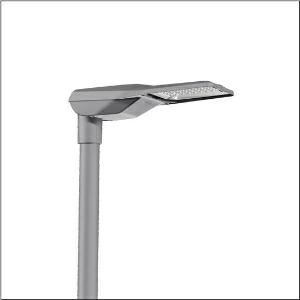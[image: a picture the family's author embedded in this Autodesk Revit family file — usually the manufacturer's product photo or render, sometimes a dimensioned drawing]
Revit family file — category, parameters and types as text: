
# Revit family: streetlight_sl_21_iq_mini___stw1_0a_5xe2e31g08gb_0d22
name_source: partatom
category: Lighting Fixtures
units: mm (PartAtom-declared; Revit-internal decimal feet)

## family parameters
Cut with Voids When Loaded = No
Host = Face
Light Source = No
Part Type = Normal
Room Calculation Point = No
Round Connector Dimension = Use Diameter
Shared = No

## types (1)
- --- (1 x LED, 5680 lm, 37.1 W, 3000K)
    Apparent Load = 37 VA
    CIE Flux Codes = 38 75 98 100 100
    Color Rendering = 70
    Color Temperature = 3000K
    Default Elevation = 1800 mm
    Description = Streetlight SL 21 iQ mini, mast luminaire, primary light control with lens, of PMMA, primary optical cover: cover, of toughened safety glass, transparent, light distribution: STW1.0a, light emission: direct distribution, primary light characteristic: asymmetric, installation type: post-top, side-entry, LED, High Power LED, rated luminous flux: 5.680lm, luminous efficacy: 153lm/W, light colour: 730, colour temperature: 3000K, control: Street-Remote, Auto-Match, Temp-Guard, Lumen-Switch, Night-Set, Smart-Wire, Light-Fading, Desk-Remote (wireless, voltage-free reading and setting of iQ features in the workshop via application-optimized NFC function/RFID function), optimised constant luminous flux control (CLO 2.0), presetting dimming linear, mains connection: 220..240V, AC, 50/60Hz, start of lifetime: 37W, end of service life: 39W, reduction: 18W, luminaire housing, of diecast aluminium, powder-coated, Siteco® metallic grey (DB 702S), corrosivity category C5 mid according to DIN EN ISO 12944, please order mast flange separately, inclination adjustable: 0°, 5°, 10°, 15°, sealing non-destructively replaceable, multi-level sealing system, length: 628mm, width: 235mm, height: 110mm, mast flange for spigot size: 42mm (side-entry): 5XC10008XM4, 60/48mm (side-entry/post-top): 5XC10108XM2, 76/60mm (side-entry/post-top): 5XC10108XM1, protection rating (complete): IP66, insulation class (complete): insulation class II (safety insulation), certification: CE, ENEC, ENEC+, VDE, impact resistance: IK09, permissible operating ambient temperature for outdoor applications: -40..+50°C, standard-compliant lighting for roads and squares, packaging unit: 1 piece

Light Distribution: STW1.0a
    Height = 110 mm
    Lamp = 1 x LED
    Lamp Light Flux = 5680 lm
    Lamp Power = 37.1 W
    Lamp count = 1
    Length = 625 mm
    Luminous efficacy = 153 lm/W
    Manufacturer = Siteco
    ModVariant = No
    Model = 5XE2E31G08GB
    Number of Poles = 1
    OnlyDefault = Yes
    Power Factor = 1
    Product Name = Streetlight SL 21 iQ mini | STW1.0a
    Product group = mast luminaire | pylon top
    ProductGroupID = 6100
    Protection Class = Protection class II
    Protection Degree = IP 66
    RLX_Detail_Level = 1
    RLX_Emergency_Light_Flux = 0 lm
    RLX_Emergency_Type = 0
    RLX_Emergency_Type_DB = No
    RlxData = <blob elided: 92421 chars, md5=d124ac80>
    Socket = socket
    Standby Power = 0 W
    System Light Flux = 5680 lm
    System Power = 37 W
    Type Comments = factory setting: luminous flux: 100 % | dim-lin: 254 | 385 mA
    Type Image = l_1003519.jpg
    URL = http://relux.com
    VarID = @adj_139389
    Voltage = 0 V
    Weight = 0.00 kg
    Width = 234 mm

## geometry (parser evidence)
native form markers: Blend x4, Sweep x12
no freeform markers — native parametric forms only
